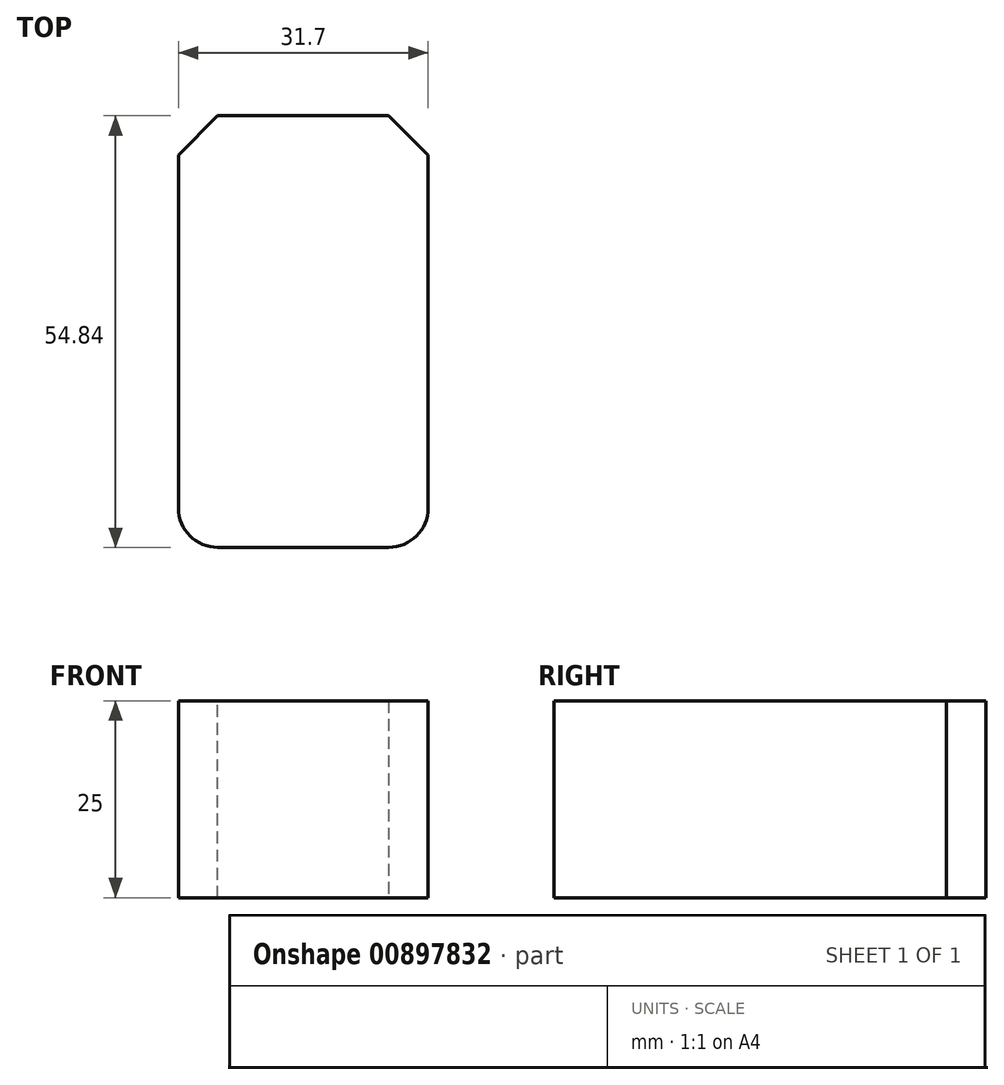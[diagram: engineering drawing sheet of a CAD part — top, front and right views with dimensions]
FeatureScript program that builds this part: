
annotation { "Feature Type Name" : "Feature", "Feature Type Description" : "" }
export const myFeature = defineFeature(function(context is Context, id is Id, definition is map)
    precondition{}
    {
        {
            var Q0;
            Q0=qCreatedBy(makeId("Top.planeOp"),FACE);
            var sketch = newSketch(context, id + "F0", { "sketchPlane" : qUnion([Q0])});
            skLineSegment(sketch, "E0.bottom", {"start": v(15.85, -27.42) * mm, "end": v(-15.85, -27.42) * mm});
            skLineSegment(sketch, "E0.top", {"start": v(15.85, 27.42) * mm, "end": v(-15.85, 27.42) * mm});
            skLineSegment(sketch, "E0.left", {"start": v(15.85, -27.42) * mm, "end": v(15.85, 27.42) * mm});
            skLineSegment(sketch, "E0.right", {"start": v(-15.85, -27.42) * mm, "end": v(-15.85, 27.42) * mm});
            skPoint(sketch, "E0.middle", {"position": v(0, 0) * mm});
            skSolve(sketch);
        }
        {
            var Q0;
            Q0 = qSketchRegion(id + "F0", true);
            extrude(context, id + "F1", {"entities" : qUnion([Q0]), "depth" : 25 * mm, "offsetDistance" : 25 * mm});
        }
        {
            var Q0;
            Q0=makeQuery(id+"F1.opExtrude","SWEPT_EDGE",EDGE,{"disambiguationData":[OSD([sQuery(id+"F0.wireOp",EDGE,"E0.top"),sQuery(id+"F0.wireOp",EDGE,"E0.left")])]});
            var Q1;
            Q1=makeQuery(id+"F1.opExtrude","SWEPT_EDGE",EDGE,{"disambiguationData":[OSD([sQuery(id+"F0.wireOp",EDGE,"E0.top"),sQuery(id+"F0.wireOp",EDGE,"E0.right")])]});
            chamfer(context, id + "F2", {"entities" : qUnion([Q0, Q1]), "width" : 5 * mm, "tangentPropagation" : true});
        }
        {
            var Q0;
            Q0=makeQuery(id+"F1.opExtrude","SWEPT_EDGE",EDGE,{"disambiguationData":[OSD([sQuery(id+"F0.wireOp",EDGE,"E0.bottom"),sQuery(id+"F0.wireOp",EDGE,"E0.right")])]});
            var Q1;
            Q1=makeQuery(id+"F1.opExtrude","SWEPT_EDGE",EDGE,{"disambiguationData":[OSD([sQuery(id+"F0.wireOp",EDGE,"E0.bottom"),sQuery(id+"F0.wireOp",EDGE,"E0.left")])]});
            fillet(context, id + "F3", {"entities" : qUnion([Q0, Q1]), "radius" : 5 * mm, "tangentPropagation" : true, "allowEdgeOverflow" : false});
        }
    });
